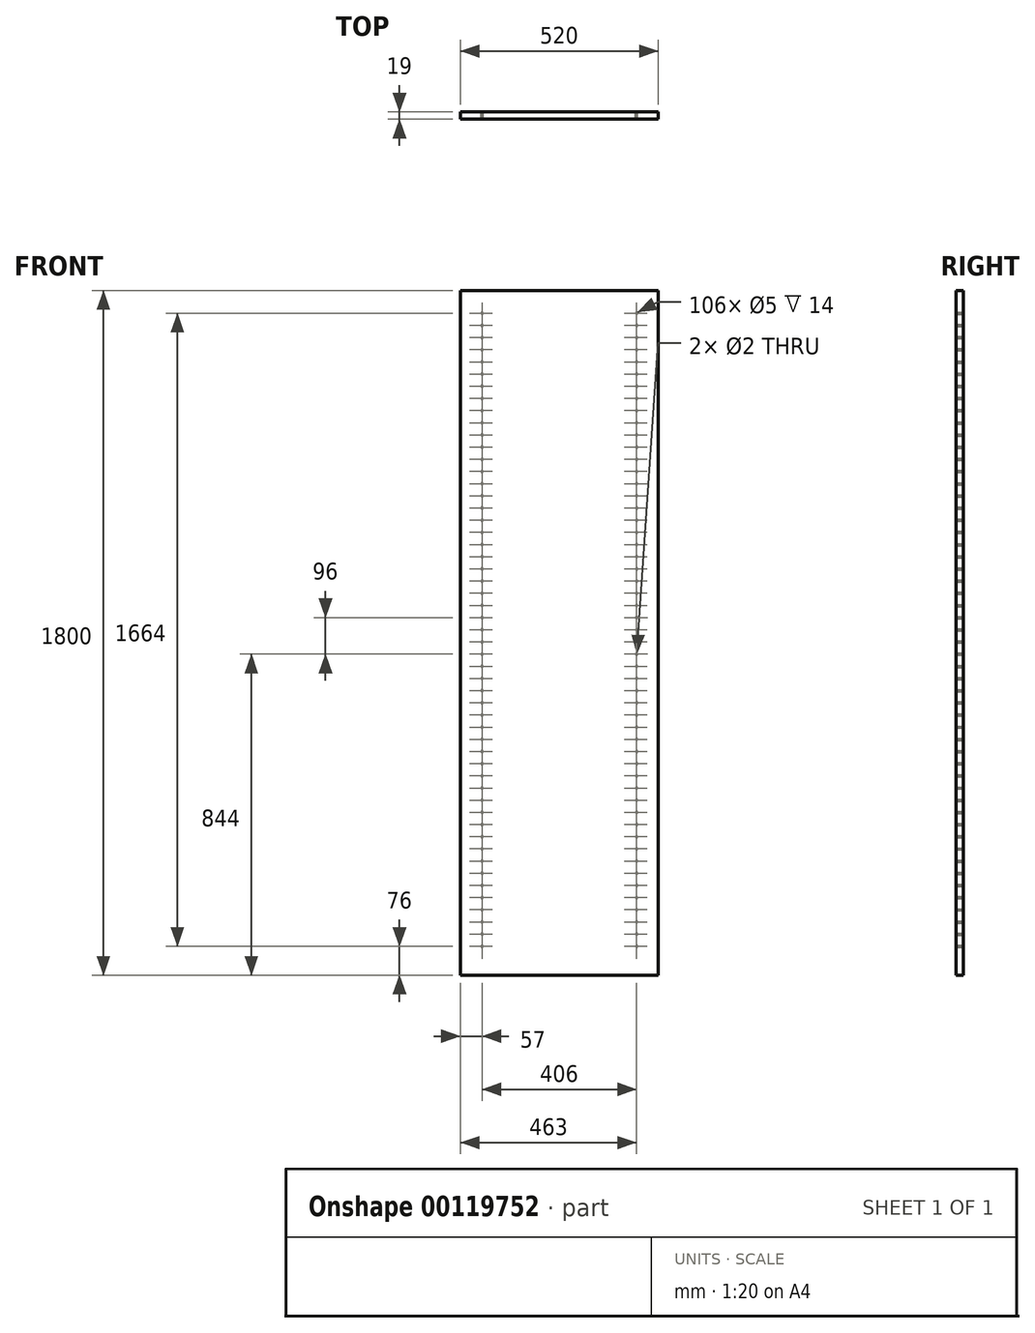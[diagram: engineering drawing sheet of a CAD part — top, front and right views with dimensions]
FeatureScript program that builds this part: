
annotation { "Feature Type Name" : "Feature", "Feature Type Description" : "" }
export const myFeature = defineFeature(function(context is Context, id is Id, definition is map)
    precondition{}
    {
        {
            var Q0;
            Q0=qCreatedBy(makeId("Front.planeOp"),FACE);
            var sketch = newSketch(context, id + "F0", { "sketchPlane" : qUnion([Q0])});
            skLineSegment(sketch, "E0.bottom", {"start": v(-260, 900) * mm, "end": v(260, 900) * mm});
            skLineSegment(sketch, "E0.top", {"start": v(-260, -900) * mm, "end": v(260, -900) * mm});
            skLineSegment(sketch, "E0.left", {"start": v(-260, 900) * mm, "end": v(-260, -900) * mm});
            skLineSegment(sketch, "E0.right", {"start": v(260, 900) * mm, "end": v(260, -900) * mm});
            skPoint(sketch, "E0.middle", {"position": v(0, 0) * mm});
            skSolve(sketch);
        }
        {
            var Q0;
            Q0=makeQuery(id+"F0.imprint","IMPRINT",FACE,{"disambiguationData":[TD([[makeQuery(id+"F0.imprint","IMPRINT",EDGE,{"derivedFrom":sQuery(id+"F0.wireOp",EDGE,"E0.bottom")}),-1.0]])]});
            extrude(context, id + "F1", {"entities" : qUnion([Q0]), "depth" : 19 * mm});
        }
        {
            var Q0;
            Q0=makeQuery(id+"F1.opExtrude","CAP_FACE",FACE,{"disambiguationData":[OSD([sQuery(id+"F0.wireOp",EDGE,"E0.bottom"),sQuery(id+"F0.wireOp",EDGE,"E0.top"),sQuery(id+"F0.wireOp",EDGE,"E0.left"),sQuery(id+"F0.wireOp",EDGE,"E0.right")])],"isStart":true});
            var sketch = newSketch(context, id + "F2", { "sketchPlane" : qUnion([Q0])});
            skCircle(sketch, "E1", {"center": v(-203, 840) * mm, "radius": 2.5 * mm});
            skCircle(sketch, "E2.0.1.0", {"center": v(-203, 808) * mm, "radius": 2.5 * mm});
            skCircle(sketch, "E2.0.2.0", {"center": v(-203, 776) * mm, "radius": 2.5 * mm});
            skCircle(sketch, "E2.0.3.0", {"center": v(-203, 744) * mm, "radius": 2.5 * mm});
            skCircle(sketch, "E2.0.4.0", {"center": v(-203, 712) * mm, "radius": 2.5 * mm});
            skCircle(sketch, "E2.0.5.0", {"center": v(-203, 680) * mm, "radius": 2.5 * mm});
            skCircle(sketch, "E2.0.6.0", {"center": v(-203, 648) * mm, "radius": 2.5 * mm});
            skCircle(sketch, "E2.0.7.0", {"center": v(-203, 616) * mm, "radius": 2.5 * mm});
            skCircle(sketch, "E2.0.8.0", {"center": v(-203, 584) * mm, "radius": 2.5 * mm});
            skCircle(sketch, "E2.0.9.0", {"center": v(-203, 552) * mm, "radius": 2.5 * mm});
            skCircle(sketch, "E2.0.10.0", {"center": v(-203, 520) * mm, "radius": 2.5 * mm});
            skCircle(sketch, "E2.0.11.0", {"center": v(-203, 488) * mm, "radius": 2.5 * mm});
            skCircle(sketch, "E2.0.12.0", {"center": v(-203, 456) * mm, "radius": 2.5 * mm});
            skCircle(sketch, "E2.0.13.0", {"center": v(-203, 424) * mm, "radius": 2.5 * mm});
            skCircle(sketch, "E2.0.14.0", {"center": v(-203, 392) * mm, "radius": 2.5 * mm});
            skCircle(sketch, "E2.0.15.0", {"center": v(-203, 360) * mm, "radius": 2.5 * mm});
            skCircle(sketch, "E2.0.16.0", {"center": v(-203, 328) * mm, "radius": 2.5 * mm});
            skCircle(sketch, "E2.0.17.0", {"center": v(-203, 296) * mm, "radius": 2.5 * mm});
            skCircle(sketch, "E2.0.18.0", {"center": v(-203, 264) * mm, "radius": 2.5 * mm});
            skCircle(sketch, "E2.0.19.0", {"center": v(-203, 232) * mm, "radius": 2.5 * mm});
            skCircle(sketch, "E2.0.20.0", {"center": v(-203, 200) * mm, "radius": 2.5 * mm});
            skCircle(sketch, "E2.0.21.0", {"center": v(-203, 168) * mm, "radius": 2.5 * mm});
            skCircle(sketch, "E2.0.22.0", {"center": v(-203, 136) * mm, "radius": 2.5 * mm});
            skCircle(sketch, "E2.0.23.0", {"center": v(-203, 104) * mm, "radius": 2.5 * mm});
            skCircle(sketch, "E2.0.24.0", {"center": v(-203, 72) * mm, "radius": 2.5 * mm});
            skCircle(sketch, "E2.0.25.0", {"center": v(-203, 40) * mm, "radius": 2.5 * mm});
            skCircle(sketch, "E2.0.26.0", {"center": v(-203, 8) * mm, "radius": 2.5 * mm});
            skCircle(sketch, "E2.0.27.0", {"center": v(-203, -24) * mm, "radius": 2.5 * mm});
            skCircle(sketch, "E2.0.28.0", {"center": v(-203, -56) * mm, "radius": 2.5 * mm});
            skCircle(sketch, "E2.0.29.0", {"center": v(-203, -88) * mm, "radius": 2.5 * mm});
            skCircle(sketch, "E2.0.30.0", {"center": v(-203, -120) * mm, "radius": 2.5 * mm});
            skCircle(sketch, "E2.0.31.0", {"center": v(-203, -152) * mm, "radius": 2.5 * mm});
            skCircle(sketch, "E2.0.32.0", {"center": v(-203, -184) * mm, "radius": 2.5 * mm});
            skCircle(sketch, "E2.0.33.0", {"center": v(-203, -216) * mm, "radius": 2.5 * mm});
            skCircle(sketch, "E2.0.34.0", {"center": v(-203, -248) * mm, "radius": 2.5 * mm});
            skCircle(sketch, "E2.0.35.0", {"center": v(-203, -280) * mm, "radius": 2.5 * mm});
            skCircle(sketch, "E2.0.36.0", {"center": v(-203, -312) * mm, "radius": 2.5 * mm});
            skCircle(sketch, "E2.0.37.0", {"center": v(-203, -344) * mm, "radius": 2.5 * mm});
            skCircle(sketch, "E2.0.38.0", {"center": v(-203, -376) * mm, "radius": 2.5 * mm});
            skCircle(sketch, "E2.0.39.0", {"center": v(-203, -408) * mm, "radius": 2.5 * mm});
            skCircle(sketch, "E2.0.40.0", {"center": v(-203, -440) * mm, "radius": 2.5 * mm});
            skCircle(sketch, "E2.0.41.0", {"center": v(-203, -472) * mm, "radius": 2.5 * mm});
            skCircle(sketch, "E2.0.42.0", {"center": v(-203, -504) * mm, "radius": 2.5 * mm});
            skCircle(sketch, "E2.0.43.0", {"center": v(-203, -536) * mm, "radius": 2.5 * mm});
            skCircle(sketch, "E2.0.44.0", {"center": v(-203, -568) * mm, "radius": 2.5 * mm});
            skCircle(sketch, "E2.0.45.0", {"center": v(-203, -600) * mm, "radius": 2.5 * mm});
            skCircle(sketch, "E2.0.46.0", {"center": v(-203, -632) * mm, "radius": 2.5 * mm});
            skCircle(sketch, "E2.0.47.0", {"center": v(-203, -664) * mm, "radius": 2.5 * mm});
            skCircle(sketch, "E2.0.48.0", {"center": v(-203, -696) * mm, "radius": 2.5 * mm});
            skCircle(sketch, "E2.0.49.0", {"center": v(-203, -728) * mm, "radius": 2.5 * mm});
            skCircle(sketch, "E2.1.0.0", {"center": v(203, 840) * mm, "radius": 2.5 * mm});
            skCircle(sketch, "E2.1.1.0", {"center": v(203, 808) * mm, "radius": 2.5 * mm});
            skCircle(sketch, "E2.1.2.0", {"center": v(203, 776) * mm, "radius": 2.5 * mm});
            skCircle(sketch, "E2.1.3.0", {"center": v(203, 744) * mm, "radius": 2.5 * mm});
            skCircle(sketch, "E2.1.4.0", {"center": v(203, 712) * mm, "radius": 2.5 * mm});
            skCircle(sketch, "E2.1.5.0", {"center": v(203, 680) * mm, "radius": 2.5 * mm});
            skCircle(sketch, "E2.1.6.0", {"center": v(203, 648) * mm, "radius": 2.5 * mm});
            skCircle(sketch, "E2.1.7.0", {"center": v(203, 616) * mm, "radius": 2.5 * mm});
            skCircle(sketch, "E2.1.8.0", {"center": v(203, 584) * mm, "radius": 2.5 * mm});
            skCircle(sketch, "E2.1.9.0", {"center": v(203, 552) * mm, "radius": 2.5 * mm});
            skCircle(sketch, "E2.1.10.0", {"center": v(203, 520) * mm, "radius": 2.5 * mm});
            skCircle(sketch, "E2.1.11.0", {"center": v(203, 488) * mm, "radius": 2.5 * mm});
            skCircle(sketch, "E2.1.12.0", {"center": v(203, 456) * mm, "radius": 2.5 * mm});
            skCircle(sketch, "E2.1.13.0", {"center": v(203, 424) * mm, "radius": 2.5 * mm});
            skCircle(sketch, "E2.1.14.0", {"center": v(203, 392) * mm, "radius": 2.5 * mm});
            skCircle(sketch, "E2.1.15.0", {"center": v(203, 360) * mm, "radius": 2.5 * mm});
            skCircle(sketch, "E2.1.16.0", {"center": v(203, 328) * mm, "radius": 2.5 * mm});
            skCircle(sketch, "E2.1.17.0", {"center": v(203, 296) * mm, "radius": 2.5 * mm});
            skCircle(sketch, "E2.1.18.0", {"center": v(203, 264) * mm, "radius": 2.5 * mm});
            skCircle(sketch, "E2.1.19.0", {"center": v(203, 232) * mm, "radius": 2.5 * mm});
            skCircle(sketch, "E2.1.20.0", {"center": v(203, 200) * mm, "radius": 2.5 * mm});
            skCircle(sketch, "E2.1.21.0", {"center": v(203, 168) * mm, "radius": 2.5 * mm});
            skCircle(sketch, "E2.1.22.0", {"center": v(203, 136) * mm, "radius": 2.5 * mm});
            skCircle(sketch, "E2.1.23.0", {"center": v(203, 104) * mm, "radius": 2.5 * mm});
            skCircle(sketch, "E2.1.24.0", {"center": v(203, 72) * mm, "radius": 2.5 * mm});
            skCircle(sketch, "E2.1.25.0", {"center": v(203, 40) * mm, "radius": 2.5 * mm});
            skCircle(sketch, "E2.1.26.0", {"center": v(203, 8) * mm, "radius": 2.5 * mm});
            skCircle(sketch, "E2.1.27.0", {"center": v(203, -24) * mm, "radius": 2.5 * mm});
            skCircle(sketch, "E2.1.28.0", {"center": v(203, -56) * mm, "radius": 2.5 * mm});
            skCircle(sketch, "E2.1.29.0", {"center": v(203, -88) * mm, "radius": 2.5 * mm});
            skCircle(sketch, "E2.1.30.0", {"center": v(203, -120) * mm, "radius": 2.5 * mm});
            skCircle(sketch, "E2.1.31.0", {"center": v(203, -152) * mm, "radius": 2.5 * mm});
            skCircle(sketch, "E2.1.32.0", {"center": v(203, -184) * mm, "radius": 2.5 * mm});
            skCircle(sketch, "E2.1.33.0", {"center": v(203, -216) * mm, "radius": 2.5 * mm});
            skCircle(sketch, "E2.1.34.0", {"center": v(203, -248) * mm, "radius": 2.5 * mm});
            skCircle(sketch, "E2.1.35.0", {"center": v(203, -280) * mm, "radius": 2.5 * mm});
            skCircle(sketch, "E2.1.36.0", {"center": v(203, -312) * mm, "radius": 2.5 * mm});
            skCircle(sketch, "E2.1.37.0", {"center": v(203, -344) * mm, "radius": 2.5 * mm});
            skCircle(sketch, "E2.1.38.0", {"center": v(203, -376) * mm, "radius": 2.5 * mm});
            skCircle(sketch, "E2.1.39.0", {"center": v(203, -408) * mm, "radius": 2.5 * mm});
            skCircle(sketch, "E2.1.40.0", {"center": v(203, -440) * mm, "radius": 2.5 * mm});
            skCircle(sketch, "E2.1.41.0", {"center": v(203, -472) * mm, "radius": 2.5 * mm});
            skCircle(sketch, "E2.1.42.0", {"center": v(203, -504) * mm, "radius": 2.5 * mm});
            skCircle(sketch, "E2.1.43.0", {"center": v(203, -536) * mm, "radius": 2.5 * mm});
            skCircle(sketch, "E2.1.44.0", {"center": v(203, -568) * mm, "radius": 2.5 * mm});
            skCircle(sketch, "E2.1.45.0", {"center": v(203, -600) * mm, "radius": 2.5 * mm});
            skCircle(sketch, "E2.1.46.0", {"center": v(203, -632) * mm, "radius": 2.5 * mm});
            skCircle(sketch, "E2.1.47.0", {"center": v(203, -664) * mm, "radius": 2.5 * mm});
            skCircle(sketch, "E2.1.48.0", {"center": v(203, -696) * mm, "radius": 2.5 * mm});
            skCircle(sketch, "E2.1.49.0", {"center": v(203, -728) * mm, "radius": 2.5 * mm});
            skLineSegment(sketch, "E2.direction1", {"start": v(-203, 840) * mm, "end": v(203, 840) * mm, "construction": true});
            skLineSegment(sketch, "E2.direction2", {"start": v(-203, 840) * mm, "end": v(-203, 808) * mm, "construction": true});
            skCircle(sketch, "E3.0.0.50", {"center": v(-203, -760) * mm, "radius": 2.5 * mm});
            skCircle(sketch, "E3.0.0.51", {"center": v(-203, -792) * mm, "radius": 2.5 * mm});
            skCircle(sketch, "E3.0.0.52", {"center": v(-203, -824) * mm, "radius": 2.5 * mm});
            skCircle(sketch, "E3.0.1.50", {"center": v(203, -760) * mm, "radius": 2.5 * mm});
            skCircle(sketch, "E3.0.1.51", {"center": v(203, -792) * mm, "radius": 2.5 * mm});
            skCircle(sketch, "E3.0.1.52", {"center": v(203, -824) * mm, "radius": 2.5 * mm});
            skSolve(sketch);
        }
        {
            var Q0;
            Q0=qSketchRegion(id+"F2",true);
            extrude(context, id + "F3", {"entities" : qUnion([Q0]), "operationType" : NewBodyOperationType.REMOVE, "oppositeDirection" : true, "depth" : 14 * mm});
        }
        {
            var Q0;
            Q0=makeQuery(id+"F1.opExtrude","CAP_FACE",FACE,{"disambiguationData":[OSD([sQuery(id+"F0.wireOp",EDGE,"E0.bottom"),sQuery(id+"F0.wireOp",EDGE,"E0.top"),sQuery(id+"F0.wireOp",EDGE,"E0.left"),sQuery(id+"F0.wireOp",EDGE,"E0.right")])],"isStart":false});
            var sketch = newSketch(context, id + "F4", { "sketchPlane" : qUnion([Q0])});
            skLineSegment(sketch, "E4", {"start": v(203, 40) * mm, "end": v(203, -56) * mm, "construction": true});
            skCircle(sketch, "E5", {"center": v(203, 40) * mm, "radius": 1 * mm});
            skCircle(sketch, "E6", {"center": v(203, -56) * mm, "radius": 1 * mm});
            skSolve(sketch);
        }
        {
            var Q0;
            Q0=qSketchRegion(id+"F4",true);
            extrude(context, id + "F5", {"entities" : qUnion([Q0]), "operationType" : NewBodyOperationType.REMOVE, "endBound" : BoundingType.THROUGH_ALL, "oppositeDirection" : true, "depth" : 25 * mm});
        }
    });
